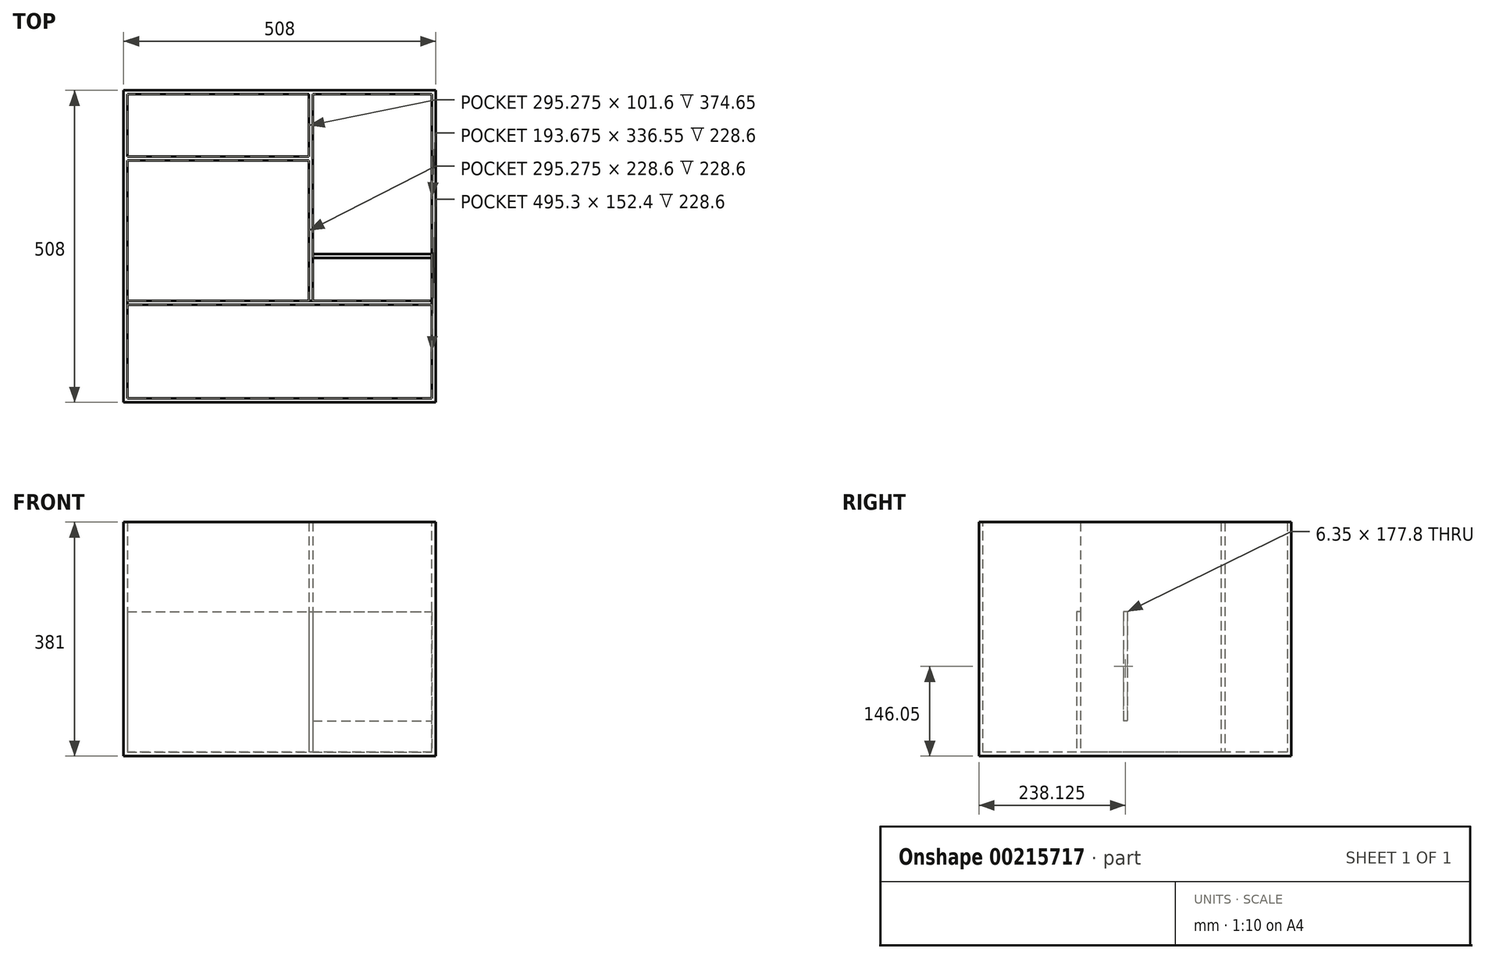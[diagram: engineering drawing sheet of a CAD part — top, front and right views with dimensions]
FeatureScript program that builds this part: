
annotation { "Feature Type Name" : "Feature", "Feature Type Description" : "" }
export const myFeature = defineFeature(function(context is Context, id is Id, definition is map)
    precondition{}
    {
        {
            var Q0;
            Q0=qCreatedBy(makeId("Top.planeOp"),FACE);
            var sketch = newSketch(context, id + "F0", { "sketchPlane" : qUnion([Q0])});
            skLineSegment(sketch, "E0.bottom", {"start": v(254, 254) * mm, "end": v(-254, 254) * mm});
            skLineSegment(sketch, "E0.top", {"start": v(254, -254) * mm, "end": v(-254, -254) * mm});
            skLineSegment(sketch, "E0.left", {"start": v(254, 254) * mm, "end": v(254, -254) * mm});
            skLineSegment(sketch, "E0.right", {"start": v(-254, 254) * mm, "end": v(-254, -254) * mm});
            skPoint(sketch, "E0.middle", {"position": v(0, 0) * mm});
            skSolve(sketch);
        }
        {
            var Q0;
            Q0 = qSketchRegion(id + "F0", true);
            extrude(context, id + "F1", {"entities" : qUnion([Q0]), "depth" : 381 * mm});
        }
        {
            var Q0;
            Q0=makeQuery(id+"F1.opExtrude","CAP_FACE",FACE,{"disambiguationData":[OSD([sQuery(id+"F0.wireOp",EDGE,"E0.bottom"),sQuery(id+"F0.wireOp",EDGE,"E0.top"),sQuery(id+"F0.wireOp",EDGE,"E0.left"),sQuery(id+"F0.wireOp",EDGE,"E0.right")])],"isStart":false});
            var sketch = newSketch(context, id + "F2", { "sketchPlane" : qUnion([Q0])});
            skLineSegment(sketch, "E1.0", {"start": v(-247.65, 247.65) * mm, "end": v(-247.65, -247.65) * mm});
            skLineSegment(sketch, "E1.1", {"start": v(247.65, 247.65) * mm, "end": v(-247.65, 247.65) * mm});
            skLineSegment(sketch, "E1.2", {"start": v(247.65, 247.65) * mm, "end": v(247.65, -247.65) * mm});
            skLineSegment(sketch, "E1.3", {"start": v(247.65, -247.65) * mm, "end": v(-247.65, -247.65) * mm});
            skSolve(sketch);
        }
        {
            var Q0;
            Q0 = qSketchRegion(id + "F2", true);
            extrude(context, id + "F3", {"entities" : qUnion([Q0]), "operationType" : NewBodyOperationType.REMOVE, "oppositeDirection" : true, "depth" : 374.65 * mm});
        }
        {
            var Q0;
            Q0=makeQuery(id+"F3.boolean.opBoolean","COPY",FACE,{"derivedFrom":makeQuery(id+"F3.opExtrude","CAP_FACE",FACE,{"disambiguationData":[OSD([sQuery(id+"F2.wireOp",EDGE,"E1.0"),sQuery(id+"F2.wireOp",EDGE,"E1.1"),sQuery(id+"F2.wireOp",EDGE,"E1.2"),sQuery(id+"F2.wireOp",EDGE,"E1.3")])],"isStart":false})});
            var sketch = newSketch(context, id + "F4", { "sketchPlane" : qUnion([Q0])});
            skLineSegment(sketch, "E2", {"start": v(-247.65, -95.25) * mm, "end": v(247.65, -95.25) * mm});
            skLineSegment(sketch, "E3.0", {"start": v(-247.65, -88.9) * mm, "end": v(247.65, -88.9) * mm});
            skLineSegment(sketch, "E4", {"start": v(-247.65, -88.9) * mm, "end": v(-247.65, -95.25) * mm});
            skLineSegment(sketch, "E5", {"start": v(247.65, -88.9) * mm, "end": v(247.65, -95.25) * mm});
            skSolve(sketch);
        }
        {
            var Q0;
            Q0=makeQuery(id+"F4.imprint","IMPRINT",FACE,{"disambiguationData":[TD([[makeQuery(id+"F4.imprint","IMPRINT",EDGE,{"derivedFrom":sQuery(id+"F4.wireOp",EDGE,"E2")}),1.0]])]});
            extrude(context, id + "F5", {"entities" : qUnion([Q0]), "operationType" : NewBodyOperationType.ADD, "depth" : 228.6 * mm});
        }
        {
            var Q0;
            {var subQ0=sQuery(id+"F2.wireOp",EDGE,"E1.0");var subQ1=sQuery(id+"F2.wireOp",EDGE,"E1.1");var subQ2=sQuery(id+"F2.wireOp",EDGE,"E1.2");Q0=makeQuery(id+"F5.boolean.opBoolean","SPLIT",FACE,{"disambiguationData":[TD([makeQuery(id+"F3.boolean.opBoolean","COPY",FACE,{"derivedFrom":makeQuery(id+"F3.opExtrude","SWEPT_FACE",FACE,{"disambiguationData":[OSD([subQ1])]})})])],"derivedFrom":makeQuery(id+"F3.boolean.opBoolean","COPY",FACE,{"derivedFrom":makeQuery(id+"F3.opExtrude","CAP_FACE",FACE,{"disambiguationData":[OSD([subQ0,subQ1,subQ2,sQuery(id+"F2.wireOp",EDGE,"E1.3")])],"isStart":false})})});}
            var sketch = newSketch(context, id + "F6", { "sketchPlane" : qUnion([Q0])});
            skLineSegment(sketch, "E6", {"start": v(53.97, 247.65) * mm, "end": v(53.97, -88.9) * mm});
            skLineSegment(sketch, "E7", {"start": v(53.97, -12.7) * mm, "end": v(247.65, -12.7) * mm});
            skLineSegment(sketch, "E8", {"start": v(-247.65, 139.7) * mm, "end": v(47.62, 139.7) * mm});
            skLineSegment(sketch, "E9.0", {"start": v(47.62, 247.65) * mm, "end": v(47.62, -88.9) * mm});
            skLineSegment(sketch, "E10.0", {"start": v(53.97, -19.05) * mm, "end": v(247.65, -19.05) * mm});
            skLineSegment(sketch, "E11.0", {"start": v(-247.65, 146.05) * mm, "end": v(47.62, 146.05) * mm});
            skLineSegment(sketch, "E12", {"start": v(53.97, -88.9) * mm, "end": v(47.62, -88.9) * mm});
            skLineSegment(sketch, "E13", {"start": v(47.62, 247.65) * mm, "end": v(53.97, 247.65) * mm});
            skLineSegment(sketch, "E14", {"start": v(53.97, -19.05) * mm, "end": v(53.97, -12.7) * mm});
            skLineSegment(sketch, "E15", {"start": v(247.65, -19.05) * mm, "end": v(247.65, -12.7) * mm});
            skSolve(sketch);
        }
        {
            var Q0;
            {var subQ0=sQuery(id+"F6.wireOp",EDGE,"E7");Q0=makeQuery(id+"F6.imprint","IMPRINT",FACE,{"disambiguationData":[TD([[makeQuery(id+"F6.imprint","IMPRINT",EDGE,{"derivedFrom":subQ0}),-1.0]])]});}
            extrude(context, id + "F7", {"entities" : qUnion([Q0]), "operationType" : NewBodyOperationType.ADD, "depth" : 228.6 * mm});
        }
        {
            var Q0;
            {var subQ0=sQuery(id+"F6.wireOp",EDGE,"E12");Q0=makeQuery(id+"F6.imprint","IMPRINT",FACE,{"disambiguationData":[TD([[makeQuery(id+"F6.imprint","IMPRINT",EDGE,{"derivedFrom":subQ0}),1.0]])]});}
            extrude(context, id + "F8", {"entities" : qUnion([Q0]), "operationType" : NewBodyOperationType.ADD, "depth" : 374.65 * mm});
        }
        {
            var Q0;
            {var subQ0=sQuery(id+"F6.wireOp",EDGE,"E8");Q0=makeQuery(id+"F6.imprint","IMPRINT",FACE,{"disambiguationData":[TD([[makeQuery(id+"F6.imprint","IMPRINT",EDGE,{"derivedFrom":subQ0}),1.0]])]});}
            extrude(context, id + "F9", {"entities" : qUnion([Q0]), "operationType" : NewBodyOperationType.ADD, "depth" : 374.65 * mm});
        }
        {
            var Q0;
            Q0=makeQuery(id+"F6.imprint","IMPRINT",FACE,{"disambiguationData":[TD([[makeQuery(id+"F6.imprint","IMPRINT",EDGE,{"derivedFrom":sQuery(id+"F6.wireOp",EDGE,"E7")}),-1.0]])]});
            extrude(context, id + "F10", {"entities" : qUnion([Q0]), "operationType" : NewBodyOperationType.REMOVE, "depth" : 50.8 * mm});
        }
    });
